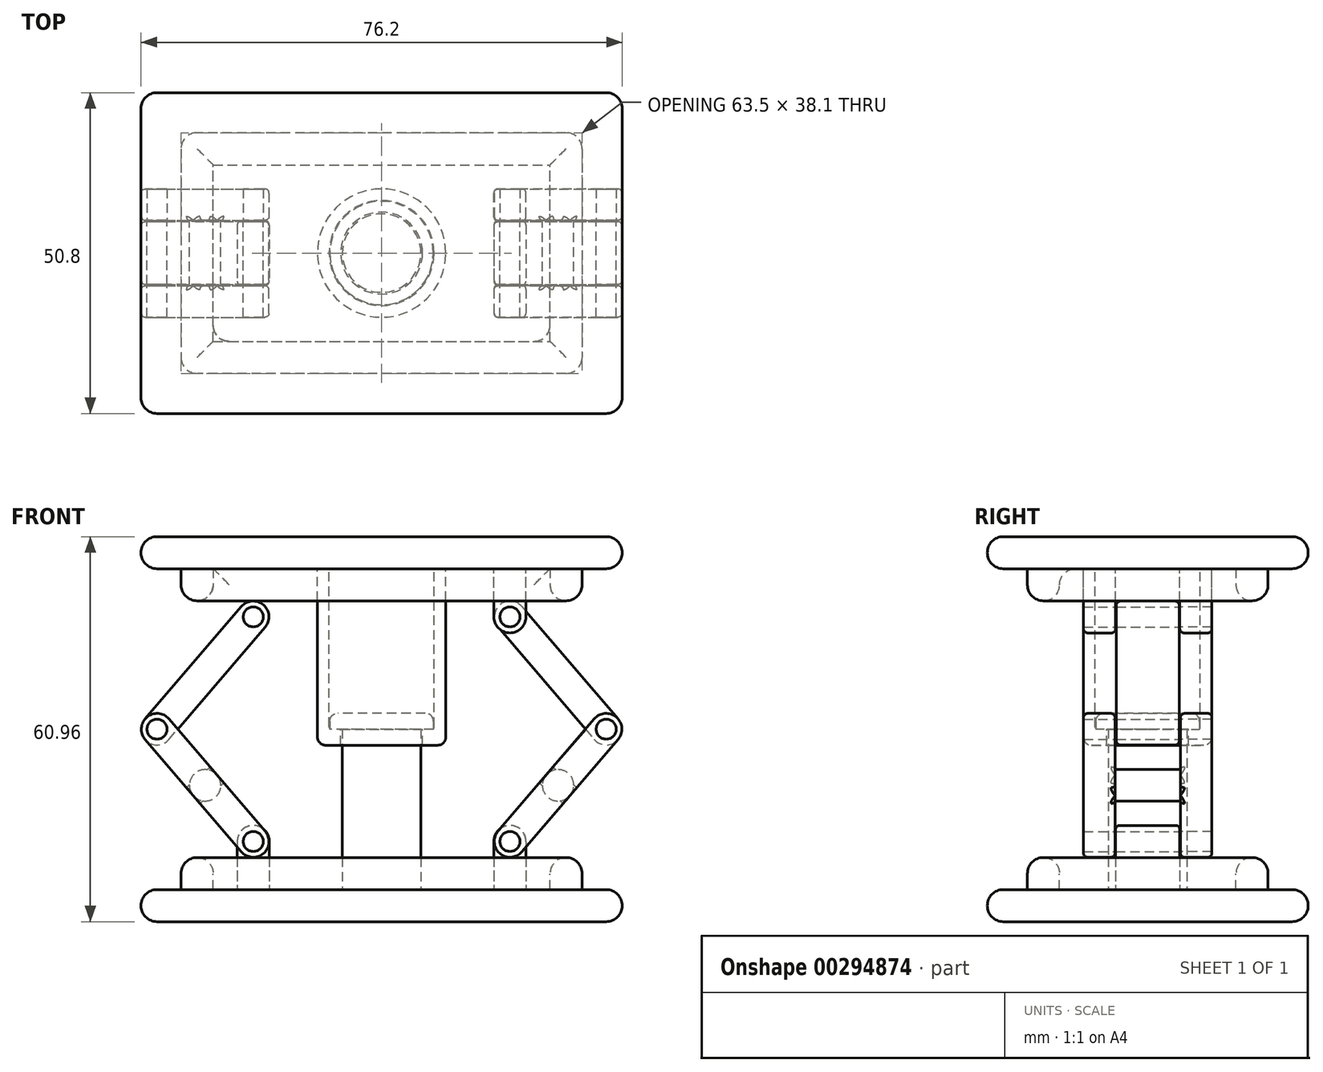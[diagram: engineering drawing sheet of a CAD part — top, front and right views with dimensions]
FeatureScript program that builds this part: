
annotation { "Feature Type Name" : "Feature", "Feature Type Description" : "" }
export const myFeature = defineFeature(function(context is Context, id is Id, definition is map)
    precondition{}
    {
        {
            var Q0;
            Q0=qCreatedBy(makeId("Top.planeOp"),FACE);
            var sketch = newSketch(context, id + "F0", { "sketchPlane" : qUnion([Q0])});
            skLineSegment(sketch, "E0.bottom", {"start": v(-38.1, 25.4) * mm, "end": v(38.1, 25.4) * mm});
            skLineSegment(sketch, "E0.top", {"start": v(-38.1, -25.4) * mm, "end": v(38.1, -25.4) * mm});
            skLineSegment(sketch, "E0.left", {"start": v(-38.1, 25.4) * mm, "end": v(-38.1, -25.4) * mm});
            skLineSegment(sketch, "E0.right", {"start": v(38.1, 25.4) * mm, "end": v(38.1, -25.4) * mm});
            skPoint(sketch, "E0.middle", {"position": v(0, 0) * mm});
            skLineSegment(sketch, "E1.bottom", {"start": v(31.75, 19.05) * mm, "end": v(-31.75, 19.05) * mm});
            skLineSegment(sketch, "E1.top", {"start": v(31.75, -19.05) * mm, "end": v(-31.75, -19.05) * mm});
            skLineSegment(sketch, "E1.left", {"start": v(31.75, 19.05) * mm, "end": v(31.75, -19.05) * mm});
            skLineSegment(sketch, "E1.right", {"start": v(-31.75, 19.05) * mm, "end": v(-31.75, -19.05) * mm});
            skLineSegment(sketch, "E2.bottom", {"start": v(-26.67, -13.97) * mm, "end": v(26.67, -13.97) * mm});
            skLineSegment(sketch, "E2.top", {"start": v(-26.67, 13.97) * mm, "end": v(26.67, 13.97) * mm});
            skLineSegment(sketch, "E2.left", {"start": v(-26.67, -13.97) * mm, "end": v(-26.67, 13.97) * mm});
            skLineSegment(sketch, "E2.right", {"start": v(26.67, -13.97) * mm, "end": v(26.67, 13.97) * mm});
            skSolve(sketch);
        }
        {
            var Q0;
            Q0=makeQuery(id+"F0.imprint","IMPRINT",FACE,{"disambiguationData":[TD([[makeQuery(id+"F0.imprint","IMPRINT",EDGE,{"derivedFrom":sQuery(id+"F0.wireOp",EDGE,"E0.bottom")}),-1.0]])]});
            var Q1;
            Q1=makeQuery(id+"F0.imprint","IMPRINT",FACE,{"disambiguationData":[TD([[makeQuery(id+"F0.imprint","IMPRINT",EDGE,{"derivedFrom":sQuery(id+"F0.wireOp",EDGE,"E2.bottom")}),1.0]])]});
            extrude(context, id + "F1", {"entities" : qUnion([Q0, Q1]), "depth" : 30.48 * mm, "hasSecondDirection" : true, "secondDirectionOppositeDirection" : false, "secondDirectionDepth" : 25.4 * mm});
        }
        {
            var Q0;
            Q0=makeQuery(id+"F0.imprint","IMPRINT",FACE,{"disambiguationData":[TD([[makeQuery(id+"F0.imprint","IMPRINT",EDGE,{"derivedFrom":sQuery(id+"F0.wireOp",EDGE,"E1.bottom")}),1.0]])]});
            extrude(context, id + "F2", {"entities" : qUnion([Q0]), "operationType" : NewBodyOperationType.ADD, "depth" : 30.48 * mm, "hasSecondDirection" : true, "secondDirectionOppositeDirection" : false, "secondDirectionDepth" : 20.32 * mm});
        }
        {
            var Q0;
            Q0=makeQuery(id+"F0.imprint","IMPRINT",FACE,{"disambiguationData":[TD([[makeQuery(id+"F0.imprint","IMPRINT",EDGE,{"derivedFrom":sQuery(id+"F0.wireOp",EDGE,"E0.bottom")}),-1.0]])]});
            var Q1;
            Q1=makeQuery(id+"F0.imprint","IMPRINT",FACE,{"disambiguationData":[TD([[makeQuery(id+"F0.imprint","IMPRINT",EDGE,{"derivedFrom":sQuery(id+"F0.wireOp",EDGE,"E2.bottom")}),1.0]])]});
            extrude(context, id + "F3", {"entities" : qUnion([Q0, Q1]), "oppositeDirection" : true, "depth" : 30.48 * mm, "hasSecondDirection" : true, "secondDirectionOppositeDirection" : true, "secondDirectionDepth" : 25.4 * mm});
        }
        {
            var Q0;
            Q0=makeQuery(id+"F0.imprint","IMPRINT",FACE,{"disambiguationData":[TD([[makeQuery(id+"F0.imprint","IMPRINT",EDGE,{"derivedFrom":sQuery(id+"F0.wireOp",EDGE,"E1.bottom")}),1.0]])]});
            extrude(context, id + "F4", {"entities" : qUnion([Q0]), "operationType" : NewBodyOperationType.ADD, "oppositeDirection" : true, "depth" : 30.48 * mm, "hasSecondDirection" : true, "secondDirectionOppositeDirection" : true, "secondDirectionDepth" : 20.32 * mm});
        }
        {
            var Q0;
            Q0=makeQuery(id+"F1.opExtrude","CAP_FACE",FACE,{"disambiguationData":[OSD([sQuery(id+"F0.wireOp",EDGE,"E2.bottom"),sQuery(id+"F0.wireOp",EDGE,"E2.top"),sQuery(id+"F0.wireOp",EDGE,"E2.left"),sQuery(id+"F0.wireOp",EDGE,"E2.right")])],"isStart":true});
            var sketch = newSketch(context, id + "F5", { "sketchPlane" : qUnion([Q0])});
            skCircle(sketch, "E3", {"center": v(0, 0) * mm, "radius": 10.16 * mm});
            skCircle(sketch, "E4", {"center": v(0, 0) * mm, "radius": 6.48 * mm});
            skCircle(sketch, "E5", {"center": v(0, 0) * mm, "radius": 8.32 * mm});
            skLineSegment(sketch, "E6.bottom", {"start": v(-17.78, 5.08) * mm, "end": v(-22.86, 5.08) * mm});
            skLineSegment(sketch, "E6.top", {"start": v(-17.78, -5.08) * mm, "end": v(-22.86, -5.08) * mm});
            skLineSegment(sketch, "E6.left", {"start": v(-17.78, 5.08) * mm, "end": v(-17.78, -5.08) * mm});
            skLineSegment(sketch, "E6.right", {"start": v(-22.86, 5.08) * mm, "end": v(-22.86, -5.08) * mm});
            skPoint(sketch, "E6.middle", {"position": v(-20.32, 0) * mm});
            skLineSegment(sketch, "E7.bottom", {"start": v(17.78, 5.08) * mm, "end": v(22.86, 5.08) * mm});
            skLineSegment(sketch, "E7.top", {"start": v(17.78, -5.08) * mm, "end": v(22.86, -5.08) * mm});
            skLineSegment(sketch, "E7.left", {"start": v(17.78, 5.08) * mm, "end": v(17.78, -5.08) * mm});
            skLineSegment(sketch, "E7.right", {"start": v(22.86, 5.08) * mm, "end": v(22.86, -5.08) * mm});
            skPoint(sketch, "E7.middle", {"position": v(20.32, 0) * mm});
            skLineSegment(sketch, "E8", {"start": v(-10.16, 0) * mm, "end": v(10.16, 0) * mm});
            skLineSegment(sketch, "E9.bottom", {"start": v(-22.86, 5.08) * mm, "end": v(-17.78, 5.08) * mm});
            skLineSegment(sketch, "E9.top", {"start": v(-22.86, 10.16) * mm, "end": v(-17.78, 10.16) * mm});
            skLineSegment(sketch, "E9.left", {"start": v(-22.86, 5.08) * mm, "end": v(-22.86, 10.16) * mm});
            skLineSegment(sketch, "E9.right", {"start": v(-17.78, 5.08) * mm, "end": v(-17.78, 10.16) * mm});
            skLineSegment(sketch, "E10.bottom", {"start": v(-22.86, -5.08) * mm, "end": v(-17.78, -5.08) * mm});
            skLineSegment(sketch, "E10.top", {"start": v(-22.86, -10.16) * mm, "end": v(-17.78, -10.16) * mm});
            skLineSegment(sketch, "E10.left", {"start": v(-22.86, -5.08) * mm, "end": v(-22.86, -10.16) * mm});
            skLineSegment(sketch, "E10.right", {"start": v(-17.78, -5.08) * mm, "end": v(-17.78, -10.16) * mm});
            skLineSegment(sketch, "E11.top", {"start": v(17.78, -10.16) * mm, "end": v(22.86, -10.16) * mm});
            skLineSegment(sketch, "E11.left", {"start": v(17.78, -5.08) * mm, "end": v(17.78, -10.16) * mm});
            skLineSegment(sketch, "E11.right", {"start": v(22.86, -5.08) * mm, "end": v(22.86, -10.16) * mm});
            skLineSegment(sketch, "E12.top", {"start": v(17.78, 10.16) * mm, "end": v(22.86, 10.16) * mm});
            skLineSegment(sketch, "E12.left", {"start": v(17.78, 5.08) * mm, "end": v(17.78, 10.16) * mm});
            skLineSegment(sketch, "E12.right", {"start": v(22.86, 5.08) * mm, "end": v(22.86, 10.16) * mm});
            skSolve(sketch);
        }
        {
            var Q0;
            Q0=makeQuery(id+"F3.opExtrude","CAP_FACE",FACE,{"disambiguationData":[OSD([sQuery(id+"F0.wireOp",EDGE,"E2.bottom"),sQuery(id+"F0.wireOp",EDGE,"E2.top"),sQuery(id+"F0.wireOp",EDGE,"E2.left"),sQuery(id+"F0.wireOp",EDGE,"E2.right")])],"isStart":true});
            var sketch = newSketch(context, id + "F6", { "sketchPlane" : qUnion([Q0])});
            skCircle(sketch, "E13", {"center": v(0, 0) * mm, "radius": 6.22 * mm});
            skCircle(sketch, "E14", {"center": v(0, 0) * mm, "radius": 8.2 * mm});
            skLineSegment(sketch, "E15.bottom", {"start": v(-22.86, 5.08) * mm, "end": v(-17.78, 5.08) * mm});
            skLineSegment(sketch, "E15.top", {"start": v(-22.86, -5.08) * mm, "end": v(-17.78, -5.08) * mm});
            skLineSegment(sketch, "E15.left", {"start": v(-22.86, 5.08) * mm, "end": v(-22.86, -5.08) * mm});
            skLineSegment(sketch, "E15.right", {"start": v(-17.78, 5.08) * mm, "end": v(-17.78, -5.08) * mm});
            skPoint(sketch, "E15.middle", {"position": v(-20.32, 0) * mm});
            skLineSegment(sketch, "E16.bottom", {"start": v(17.78, 5.08) * mm, "end": v(22.86, 5.08) * mm});
            skLineSegment(sketch, "E16.top", {"start": v(17.78, -5.08) * mm, "end": v(22.86, -5.08) * mm});
            skLineSegment(sketch, "E16.left", {"start": v(17.78, 5.08) * mm, "end": v(17.78, -5.08) * mm});
            skLineSegment(sketch, "E16.right", {"start": v(22.86, 5.08) * mm, "end": v(22.86, -5.08) * mm});
            skPoint(sketch, "E16.middle", {"position": v(20.32, 0) * mm});
            skSolve(sketch);
        }
        {
            var Q0;
            {var subQ0=sQuery(id+"F5.wireOp",EDGE,"E8");var subQ1=sQuery(id+"F5.wireOp",EDGE,"E3");var subQ2=makeQuery(id+"F5.imprint","INTERSECT",VERTEX,{"disambiguationData":[OD(0.0)],"derivedFrom":[subQ1,subQ0]});Q0=makeQuery(id+"F5.imprint","IMPRINT",FACE,{"disambiguationData":[TD([[makeQuery(id+"F5.imprint","IMPRINT",EDGE,{"disambiguationData":[TD([[subQ2,-1.0]])],"derivedFrom":subQ1}),1.0]])]});}
            extrude(context, id + "F7", {"entities" : qUnion([Q0]), "operationType" : NewBodyOperationType.ADD, "depth" : 27.94 * mm});
        }
        {
            var Q0;
            Q0=makeQuery(id+"F6.imprint","IMPRINT",FACE,{"disambiguationData":[TD([[makeQuery(id+"F6.imprint","IMPRINT",EDGE,{"derivedFrom":sQuery(id+"F6.wireOp",EDGE,"E13")}),1.0]])]});
            extrude(context, id + "F8", {"entities" : qUnion([Q0]), "operationType" : NewBodyOperationType.ADD, "depth" : 27.94 * mm});
        }
        {
            var Q0;
            {var subQ0=sQuery(id+"F5.wireOp",EDGE,"E8");var subQ1=sQuery(id+"F5.wireOp",EDGE,"E4");var subQ2=makeQuery(id+"F5.imprint","INTERSECT",VERTEX,{"disambiguationData":[OD(0.0)],"derivedFrom":[subQ1,subQ0]});Q0=makeQuery(id+"F5.imprint","IMPRINT",FACE,{"disambiguationData":[TD([[makeQuery(id+"F5.imprint","IMPRINT",EDGE,{"disambiguationData":[TD([[subQ2,-1.0]])],"derivedFrom":subQ1}),-1.0]])]});}
            extrude(context, id + "F9", {"entities" : qUnion([Q0]), "operationType" : NewBodyOperationType.ADD, "depth" : 27.94 * mm, "hasSecondDirection" : true, "secondDirectionOppositeDirection" : false, "secondDirectionDepth" : 25.4 * mm});
        }
        {
            var Q0;
            Q0=makeQuery(id+"F6.imprint","IMPRINT",FACE,{"disambiguationData":[TD([[makeQuery(id+"F6.imprint","IMPRINT",EDGE,{"derivedFrom":sQuery(id+"F6.wireOp",EDGE,"E13")}),-1.0]])]});
            extrude(context, id + "F10", {"entities" : qUnion([Q0]), "operationType" : NewBodyOperationType.ADD, "depth" : 27.94 * mm, "hasSecondDirection" : true, "secondDirectionOppositeDirection" : false, "secondDirectionDepth" : 25.4 * mm});
        }
        {
            var Q0;
            Q0=makeQuery(id+"F6.imprint","IMPRINT",FACE,{"disambiguationData":[TD([[makeQuery(id+"F6.imprint","IMPRINT",EDGE,{"derivedFrom":sQuery(id+"F6.wireOp",EDGE,"E15.bottom")}),-1.0]])]});
            var Q1;
            Q1=makeQuery(id+"F6.imprint","IMPRINT",FACE,{"disambiguationData":[TD([[makeQuery(id+"F6.imprint","IMPRINT",EDGE,{"derivedFrom":sQuery(id+"F6.wireOp",EDGE,"E16.bottom")}),-1.0]])]});
            extrude(context, id + "F11", {"entities" : qUnion([Q0, Q1]), "operationType" : NewBodyOperationType.ADD, "depth" : 10.16 * mm});
        }
        {
            var Q0;
            Q0=makeQuery(id+"F5.imprint","IMPRINT",FACE,{"disambiguationData":[TD([[makeQuery(id+"F5.imprint","IMPRINT",EDGE,{"derivedFrom":sQuery(id+"F5.wireOp",EDGE,"E9.bottom")}),1.0]])]});
            var Q1;
            Q1=makeQuery(id+"F5.imprint","IMPRINT",FACE,{"disambiguationData":[TD([[makeQuery(id+"F5.imprint","IMPRINT",EDGE,{"derivedFrom":sQuery(id+"F5.wireOp",EDGE,"E10.bottom")}),-1.0]])]});
            var Q2;
            Q2=makeQuery(id+"F5.imprint","IMPRINT",FACE,{"disambiguationData":[TD([[makeQuery(id+"F5.imprint","IMPRINT",EDGE,{"derivedFrom":sQuery(id+"F5.wireOp",EDGE,"E7.top")}),-1.0]])]});
            var Q3;
            Q3=makeQuery(id+"F5.imprint","IMPRINT",FACE,{"disambiguationData":[TD([[makeQuery(id+"F5.imprint","IMPRINT",EDGE,{"derivedFrom":sQuery(id+"F5.wireOp",EDGE,"E7.bottom")}),1.0]])]});
            extrude(context, id + "F12", {"entities" : qUnion([Q0, Q1, Q2, Q3]), "operationType" : NewBodyOperationType.ADD, "depth" : 10.16 * mm});
        }
        {
            var Q0;
            Q0=makeQuery(id+"F11.opExtrude","CAP_EDGE",EDGE,{"disambiguationData":[OSD([sQuery(id+"F6.wireOp",EDGE,"E15.left")])],"isStart":false});
            var Q1;
            Q1=makeQuery(id+"F11.opExtrude","CAP_EDGE",EDGE,{"disambiguationData":[OSD([sQuery(id+"F6.wireOp",EDGE,"E15.right")])],"isStart":false});
            var Q2;
            Q2=makeQuery(id+"F11.opExtrude","CAP_EDGE",EDGE,{"disambiguationData":[OSD([sQuery(id+"F6.wireOp",EDGE,"E16.left")])],"isStart":false});
            var Q3;
            Q3=makeQuery(id+"F11.opExtrude","CAP_EDGE",EDGE,{"disambiguationData":[OSD([sQuery(id+"F6.wireOp",EDGE,"E16.right")])],"isStart":false});
            var Q4;
            Q4=makeQuery(id+"F12.opExtrude","CAP_EDGE",EDGE,{"disambiguationData":[OSD([sQuery(id+"F5.wireOp",EDGE,"E11.left")])],"isStart":false});
            var Q5;
            Q5=makeQuery(id+"F12.opExtrude","CAP_EDGE",EDGE,{"disambiguationData":[OSD([sQuery(id+"F5.wireOp",EDGE,"E12.left")])],"isStart":false});
            var Q6;
            Q6=makeQuery(id+"F12.opExtrude","CAP_EDGE",EDGE,{"disambiguationData":[OSD([sQuery(id+"F5.wireOp",EDGE,"E10.left")])],"isStart":false});
            var Q7;
            Q7=makeQuery(id+"F12.opExtrude","CAP_EDGE",EDGE,{"disambiguationData":[OSD([sQuery(id+"F5.wireOp",EDGE,"E9.left")])],"isStart":false});
            var Q8;
            Q8=makeQuery(id+"F12.opExtrude","CAP_EDGE",EDGE,{"disambiguationData":[OSD([sQuery(id+"F5.wireOp",EDGE,"E10.right")])],"isStart":false});
            var Q9;
            Q9=makeQuery(id+"F12.opExtrude","CAP_EDGE",EDGE,{"disambiguationData":[OSD([sQuery(id+"F5.wireOp",EDGE,"E9.right")])],"isStart":false});
            var Q10;
            Q10=makeQuery(id+"F12.opExtrude","CAP_EDGE",EDGE,{"disambiguationData":[OSD([sQuery(id+"F5.wireOp",EDGE,"E12.right")])],"isStart":false});
            var Q11;
            Q11=makeQuery(id+"F12.opExtrude","CAP_EDGE",EDGE,{"disambiguationData":[OSD([sQuery(id+"F5.wireOp",EDGE,"E11.right")])],"isStart":false});
            fillet(context, id + "F13", {"entities" : qUnion([Q0, Q1, Q2, Q3, Q4, Q5, Q6, Q7, Q8, Q9, Q10, Q11]), "radius" : 2.54 * mm, "tangentPropagation" : true, "allowEdgeOverflow" : false});
        }
        {
            var Q0;
            Q0=qCreatedBy(makeId("Front.planeOp"),FACE);
            var sketch = newSketch(context, id + "F14", { "sketchPlane" : qUnion([Q0])});
            skLineSegment(sketch, "E17.bottom", {"start": v(-20.32, 17.78) * mm, "end": v(20.32, 17.78) * mm});
            skLineSegment(sketch, "E17.top", {"start": v(-20.32, -17.78) * mm, "end": v(20.32, -17.78) * mm});
            skLineSegment(sketch, "E17.left", {"start": v(-20.32, 17.78) * mm, "end": v(-20.32, -17.78) * mm});
            skLineSegment(sketch, "E17.right", {"start": v(20.32, 17.78) * mm, "end": v(20.32, -17.78) * mm});
            skPoint(sketch, "E17.middle", {"position": v(0, 0) * mm});
            skPoint(sketch, "E18", {"position": v(-20.32, 17.78) * mm});
            skPoint(sketch, "E19", {"position": v(20.32, 17.78) * mm});
            skPoint(sketch, "E20", {"position": v(20.32, -17.78) * mm});
            skPoint(sketch, "E21", {"position": v(-20.32, -17.78) * mm});
            skCircle(sketch, "E22", {"center": v(-20.32, 17.78) * mm, "radius": 2.49 * mm});
            skCircle(sketch, "E23", {"center": v(20.32, 17.78) * mm, "radius": 2.49 * mm});
            skCircle(sketch, "E24", {"center": v(20.32, -17.78) * mm, "radius": 2.49 * mm});
            skCircle(sketch, "E25", {"center": v(-20.32, -17.78) * mm, "radius": 2.49 * mm});
            skCircle(sketch, "E26", {"center": v(-35.56, 0) * mm, "radius": 2.49 * mm});
            skCircle(sketch, "E27", {"center": v(35.56, 0) * mm, "radius": 2.49 * mm});
            skLineSegment(sketch, "E28", {"start": v(-22.2, 19.4) * mm, "end": v(-37.45, 1.62) * mm});
            skLineSegment(sketch, "E29", {"start": v(-37.45, -1.62) * mm, "end": v(-22.2, -19.4) * mm});
            skLineSegment(sketch, "E30", {"start": v(-33.67, -1.62) * mm, "end": v(-18.43, 16.16) * mm});
            skLineSegment(sketch, "E31", {"start": v(-33.67, 1.62) * mm, "end": v(-18.43, -16.16) * mm});
            skLineSegment(sketch, "E32", {"start": v(18.43, 16.16) * mm, "end": v(33.67, -1.62) * mm});
            skLineSegment(sketch, "E33", {"start": v(22.2, 19.4) * mm, "end": v(37.45, 1.62) * mm});
            skLineSegment(sketch, "E34", {"start": v(37.45, -1.62) * mm, "end": v(22.2, -19.4) * mm});
            skLineSegment(sketch, "E35", {"start": v(18.43, -16.16) * mm, "end": v(33.67, 1.62) * mm});
            skCircle(sketch, "E36", {"center": v(-27.94, -8.9) * mm, "radius": 2.49 * mm});
            skPoint(sketch, "E36.first.point", {"position": v(-26.05, -7.27) * mm});
            skPoint(sketch, "E36.second.point", {"position": v(-29.83, -10.5) * mm});
            skPoint(sketch, "E36.third.point", {"position": v(-26.05, -10.5) * mm});
            skPoint(sketch, "E36.third.point.positionSnap0", {"position": v(-29.83, -10.5) * mm});
            skPoint(sketch, "E36.third.point.positionSnap1", {"position": v(-26.05, -7.27) * mm});
            skCircle(sketch, "E37", {"center": v(27.94, -8.9) * mm, "radius": 2.49 * mm});
            skPoint(sketch, "E37.first.point", {"position": v(26.05, -7.27) * mm});
            skPoint(sketch, "E37.second.point", {"position": v(29.83, -10.5) * mm});
            skPoint(sketch, "E37.third.point", {"position": v(26.05, -10.5) * mm});
            skPoint(sketch, "E37.third.point.positionSnap0", {"position": v(29.83, -10.5) * mm});
            skPoint(sketch, "E37.third.point.positionSnap1", {"position": v(26.05, -7.27) * mm});
            skSolve(sketch);
        }
        {
            var Q0;
            {var subQ0=sQuery(id+"F5.wireOp",EDGE,"E8");var subQ1=sQuery(id+"F5.wireOp",EDGE,"E3");var subQ2=makeQuery(id+"F5.imprint","INTERSECT",VERTEX,{"disambiguationData":[OD(0.0)],"derivedFrom":[subQ1,subQ0]});Q0=makeQuery(id+"F5.imprint","IMPRINT",FACE,{"disambiguationData":[TD([[makeQuery(id+"F5.imprint","IMPRINT",EDGE,{"disambiguationData":[TD([[subQ2,1.0]])],"derivedFrom":subQ1}),1.0]])]});}
            extrude(context, id + "F15", {"entities" : qUnion([Q0]), "depth" : 27.94 * mm});
        }
        {
            var Q0;
            {var subQ0=sQuery(id+"F5.wireOp",EDGE,"E8");var subQ1=sQuery(id+"F5.wireOp",EDGE,"E4");var subQ2=makeQuery(id+"F5.imprint","INTERSECT",VERTEX,{"disambiguationData":[OD(0.0)],"derivedFrom":[subQ1,subQ0]});Q0=makeQuery(id+"F5.imprint","IMPRINT",FACE,{"disambiguationData":[TD([[makeQuery(id+"F5.imprint","IMPRINT",EDGE,{"disambiguationData":[TD([[subQ2,1.0]])],"derivedFrom":subQ1}),-1.0]])]});}
            extrude(context, id + "F16", {"entities" : qUnion([Q0]), "operationType" : NewBodyOperationType.ADD, "depth" : 27.94 * mm, "hasSecondDirection" : true, "secondDirectionOppositeDirection" : false, "secondDirectionDepth" : 25.4 * mm});
        }
        {
            var Q0;
            {var subQ0=sQuery(id+"F14.wireOp",EDGE,"E28");Q0=makeQuery(id+"F14.imprint","IMPRINT",FACE,{"disambiguationData":[TD([[makeQuery(id+"F14.imprint","IMPRINT",EDGE,{"derivedFrom":subQ0}),1.0]])]});}
            var Q1;
            {var subQ0=sQuery(id+"F14.wireOp",EDGE,"E22");var subQ1=sQuery(id+"F14.wireOp",EDGE,"E17.left");var subQ2=makeQuery(id+"F14.imprint","INTERSECT",VERTEX,{"derivedFrom":[subQ1,subQ0]});Q1=makeQuery(id+"F14.imprint","IMPRINT",FACE,{"disambiguationData":[TD([[makeQuery(id+"F14.imprint","IMPRINT",EDGE,{"disambiguationData":[TD([[subQ2,-1.0]])],"derivedFrom":subQ1}),1.0]])]});}
            var Q2;
            {var subQ0=sQuery(id+"F14.wireOp",EDGE,"E17.left");var subQ1=sQuery(id+"F14.wireOp",EDGE,"E17.bottom");var subQ2=makeQuery(id+"F14.imprint","INTERSECT",VERTEX,{"derivedFrom":[subQ1,subQ0]});Q2=makeQuery(id+"F14.imprint","IMPRINT",FACE,{"disambiguationData":[TD([[makeQuery(id+"F14.imprint","IMPRINT",EDGE,{"disambiguationData":[TD([[subQ2,-1.0]])],"derivedFrom":subQ1}),-1.0]])]});}
            var Q3;
            {var subQ0=sQuery(id+"F14.wireOp",EDGE,"E17.left");var subQ1=sQuery(id+"F14.wireOp",EDGE,"E17.bottom");var subQ2=makeQuery(id+"F14.imprint","INTERSECT",VERTEX,{"derivedFrom":[subQ1,subQ0]});Q3=makeQuery(id+"F14.imprint","IMPRINT",FACE,{"disambiguationData":[TD([[makeQuery(id+"F14.imprint","IMPRINT",EDGE,{"disambiguationData":[TD([[subQ2,-1.0]])],"derivedFrom":subQ1}),1.0]])]});}
            var Q4;
            {var subQ0=sQuery(id+"F14.wireOp",EDGE,"E26");var subQ1=makeQuery(id+"F14.imprint","INTERSECT",VERTEX,{"derivedFrom":[subQ0,sQuery(id+"F14.wireOp",EDGE,"E28")]});Q4=makeQuery(id+"F14.imprint","IMPRINT",FACE,{"disambiguationData":[TD([[makeQuery(id+"F14.imprint","IMPRINT",EDGE,{"disambiguationData":[TD([[subQ1,1.0]])],"derivedFrom":subQ0}),1.0]])]});}
            var Q5;
            {var subQ0=sQuery(id+"F14.wireOp",EDGE,"E30");var subQ1=sQuery(id+"F14.wireOp",EDGE,"E26");var subQ2=makeQuery(id+"F14.imprint","INTERSECT",VERTEX,{"derivedFrom":[subQ1,subQ0]});Q5=makeQuery(id+"F14.imprint","IMPRINT",FACE,{"disambiguationData":[TD([[makeQuery(id+"F14.imprint","IMPRINT",EDGE,{"disambiguationData":[TD([[subQ2,-1.0]])],"derivedFrom":subQ1}),-1.0]])]});}
            var Q6;
            {var subQ0=sQuery(id+"F14.wireOp",EDGE,"E23");var subQ1=sQuery(id+"F14.wireOp",EDGE,"E17.right");var subQ2=makeQuery(id+"F14.imprint","INTERSECT",VERTEX,{"derivedFrom":[subQ1,subQ0]});Q6=makeQuery(id+"F14.imprint","IMPRINT",FACE,{"disambiguationData":[TD([[makeQuery(id+"F14.imprint","IMPRINT",EDGE,{"disambiguationData":[TD([[subQ2,-1.0]])],"derivedFrom":subQ1}),-1.0]])]});}
            var Q7;
            {var subQ5=sQuery(id+"F14.wireOp",EDGE,"E33");Q7=makeQuery(id+"F14.imprint","IMPRINT",FACE,{"disambiguationData":[TD([[makeQuery(id+"F14.imprint","IMPRINT",EDGE,{"derivedFrom":subQ5}),-1.0]])]});}
            var Q8;
            {var subQ0=sQuery(id+"F14.wireOp",EDGE,"E32");var subQ1=sQuery(id+"F14.wireOp",EDGE,"E27");var subQ2=makeQuery(id+"F14.imprint","INTERSECT",VERTEX,{"derivedFrom":[subQ1,subQ0]});Q8=makeQuery(id+"F14.imprint","IMPRINT",FACE,{"disambiguationData":[TD([[makeQuery(id+"F14.imprint","IMPRINT",EDGE,{"disambiguationData":[TD([[subQ2,1.0]])],"derivedFrom":subQ1}),-1.0]])]});}
            var Q9;
            {var subQ0=sQuery(id+"F14.wireOp",EDGE,"E27");var subQ1=makeQuery(id+"F14.imprint","INTERSECT",VERTEX,{"derivedFrom":[subQ0,sQuery(id+"F14.wireOp",EDGE,"E33")]});Q9=makeQuery(id+"F14.imprint","IMPRINT",FACE,{"disambiguationData":[TD([[makeQuery(id+"F14.imprint","IMPRINT",EDGE,{"disambiguationData":[TD([[subQ1,-1.0]])],"derivedFrom":subQ0}),1.0]])]});}
            var Q10;
            {var subQ0=sQuery(id+"F14.wireOp",EDGE,"E17.right");var subQ1=sQuery(id+"F14.wireOp",EDGE,"E17.bottom");var subQ2=makeQuery(id+"F14.imprint","INTERSECT",VERTEX,{"derivedFrom":[subQ1,subQ0]});Q10=makeQuery(id+"F14.imprint","IMPRINT",FACE,{"disambiguationData":[TD([[makeQuery(id+"F14.imprint","IMPRINT",EDGE,{"disambiguationData":[TD([[subQ2,1.0]])],"derivedFrom":subQ1}),1.0]])]});}
            var Q11;
            {var subQ0=sQuery(id+"F14.wireOp",EDGE,"E17.right");var subQ1=sQuery(id+"F14.wireOp",EDGE,"E17.bottom");var subQ2=makeQuery(id+"F14.imprint","INTERSECT",VERTEX,{"derivedFrom":[subQ1,subQ0]});Q11=makeQuery(id+"F14.imprint","IMPRINT",FACE,{"disambiguationData":[TD([[makeQuery(id+"F14.imprint","IMPRINT",EDGE,{"disambiguationData":[TD([[subQ2,1.0]])],"derivedFrom":subQ1}),-1.0]])]});}
            extrude(context, id + "F17", {"entities" : qUnion([Q0, Q1, Q2, Q3, Q4, Q5, Q6, Q7, Q8, Q9, Q10, Q11]), "depth" : 9.96 * mm, "symmetric" : true});
        }
        {
            var Q0;
            {var subQ0=sQuery(id+"F14.wireOp",EDGE,"E36");var subQ1=makeQuery(id+"F14.imprint","INTERSECT",VERTEX,{"derivedFrom":[sQuery(id+"F14.wireOp",EDGE,"E29"),subQ0]});Q0=makeQuery(id+"F14.imprint","IMPRINT",FACE,{"disambiguationData":[TD([[makeQuery(id+"F14.imprint","IMPRINT",EDGE,{"disambiguationData":[TD([[subQ1,1.0]])],"derivedFrom":subQ0}),1.0]])]});}
            var Q1;
            {var subQ0=sQuery(id+"F14.wireOp",EDGE,"E31");var subQ1=sQuery(id+"F14.wireOp",EDGE,"E17.left");var subQ2=makeQuery(id+"F14.imprint","INTERSECT",VERTEX,{"derivedFrom":[subQ1,subQ0]});Q1=makeQuery(id+"F14.imprint","IMPRINT",FACE,{"disambiguationData":[TD([[makeQuery(id+"F14.imprint","IMPRINT",EDGE,{"disambiguationData":[TD([[subQ2,-1.0]])],"derivedFrom":subQ1}),-1.0]])]});}
            var Q2;
            {var subQ0=sQuery(id+"F14.wireOp",EDGE,"E26");var subQ1=makeQuery(id+"F14.imprint","INTERSECT",VERTEX,{"derivedFrom":[subQ0,sQuery(id+"F14.wireOp",EDGE,"E28")]});Q2=makeQuery(id+"F14.imprint","IMPRINT",FACE,{"disambiguationData":[TD([[makeQuery(id+"F14.imprint","IMPRINT",EDGE,{"disambiguationData":[TD([[subQ1,1.0]])],"derivedFrom":subQ0}),1.0]])]});}
            var Q3;
            {var subQ5=sQuery(id+"F14.wireOp",EDGE,"E26");var subQ7=sQuery(id+"F14.wireOp",EDGE,"E29");var subQ8=makeQuery(id+"F14.imprint","INTERSECT",VERTEX,{"derivedFrom":[subQ5,subQ7]});Q3=makeQuery(id+"F14.imprint","IMPRINT",FACE,{"disambiguationData":[TD([[makeQuery(id+"F14.imprint","IMPRINT",EDGE,{"disambiguationData":[TD([[subQ8,-1.0]])],"derivedFrom":subQ5}),-1.0]])]});}
            var Q4;
            {var subQ0=sQuery(id+"F14.wireOp",EDGE,"E30");var subQ1=sQuery(id+"F14.wireOp",EDGE,"E26");var subQ2=makeQuery(id+"F14.imprint","INTERSECT",VERTEX,{"derivedFrom":[subQ1,subQ0]});Q4=makeQuery(id+"F14.imprint","IMPRINT",FACE,{"disambiguationData":[TD([[makeQuery(id+"F14.imprint","IMPRINT",EDGE,{"disambiguationData":[TD([[subQ2,-1.0]])],"derivedFrom":subQ1}),-1.0]])]});}
            var Q5;
            {var subQ0=sQuery(id+"F14.wireOp",EDGE,"E17.right");var subQ1=sQuery(id+"F14.wireOp",EDGE,"E17.top");var subQ2=makeQuery(id+"F14.imprint","INTERSECT",VERTEX,{"derivedFrom":[subQ1,subQ0]});Q5=makeQuery(id+"F14.imprint","IMPRINT",FACE,{"disambiguationData":[TD([[makeQuery(id+"F14.imprint","IMPRINT",EDGE,{"disambiguationData":[TD([[subQ2,1.0]])],"derivedFrom":subQ1}),-1.0]])]});}
            var Q6;
            {var subQ0=sQuery(id+"F14.wireOp",EDGE,"E17.right");var subQ1=sQuery(id+"F14.wireOp",EDGE,"E17.top");var subQ2=makeQuery(id+"F14.imprint","INTERSECT",VERTEX,{"derivedFrom":[subQ1,subQ0]});Q6=makeQuery(id+"F14.imprint","IMPRINT",FACE,{"disambiguationData":[TD([[makeQuery(id+"F14.imprint","IMPRINT",EDGE,{"disambiguationData":[TD([[subQ2,1.0]])],"derivedFrom":subQ1}),1.0]])]});}
            var Q7;
            {var subQ0=sQuery(id+"F14.wireOp",EDGE,"E35");var subQ1=sQuery(id+"F14.wireOp",EDGE,"E17.right");var subQ2=makeQuery(id+"F14.imprint","INTERSECT",VERTEX,{"derivedFrom":[subQ1,subQ0]});Q7=makeQuery(id+"F14.imprint","IMPRINT",FACE,{"disambiguationData":[TD([[makeQuery(id+"F14.imprint","IMPRINT",EDGE,{"disambiguationData":[TD([[subQ2,-1.0]])],"derivedFrom":subQ1}),-1.0]])]});}
            var Q8;
            {var subQ5=sQuery(id+"F14.wireOp",EDGE,"E35");var subQ6=sQuery(id+"F14.wireOp",EDGE,"E17.right");var subQ7=makeQuery(id+"F14.imprint","INTERSECT",VERTEX,{"derivedFrom":[subQ6,subQ5]});Q8=makeQuery(id+"F14.imprint","IMPRINT",FACE,{"disambiguationData":[TD([[makeQuery(id+"F14.imprint","IMPRINT",EDGE,{"disambiguationData":[TD([[subQ7,-1.0]])],"derivedFrom":subQ6}),1.0]])]});}
            var Q9;
            {var subQ0=sQuery(id+"F14.wireOp",EDGE,"E37");var subQ1=makeQuery(id+"F14.imprint","INTERSECT",VERTEX,{"derivedFrom":[sQuery(id+"F14.wireOp",EDGE,"E34"),subQ0]});Q9=makeQuery(id+"F14.imprint","IMPRINT",FACE,{"disambiguationData":[TD([[makeQuery(id+"F14.imprint","IMPRINT",EDGE,{"disambiguationData":[TD([[subQ1,1.0]])],"derivedFrom":subQ0}),1.0]])]});}
            var Q10;
            {var subQ1=sQuery(id+"F14.wireOp",EDGE,"E27");var subQ5=sQuery(id+"F14.wireOp",EDGE,"E32");var subQ6=makeQuery(id+"F14.imprint","INTERSECT",VERTEX,{"derivedFrom":[subQ1,subQ5]});Q10=makeQuery(id+"F14.imprint","IMPRINT",FACE,{"disambiguationData":[TD([[makeQuery(id+"F14.imprint","IMPRINT",EDGE,{"disambiguationData":[TD([[subQ6,-1.0]])],"derivedFrom":subQ1}),-1.0]])]});}
            var Q11;
            {var subQ0=sQuery(id+"F14.wireOp",EDGE,"E32");var subQ1=sQuery(id+"F14.wireOp",EDGE,"E27");var subQ2=makeQuery(id+"F14.imprint","INTERSECT",VERTEX,{"derivedFrom":[subQ1,subQ0]});Q11=makeQuery(id+"F14.imprint","IMPRINT",FACE,{"disambiguationData":[TD([[makeQuery(id+"F14.imprint","IMPRINT",EDGE,{"disambiguationData":[TD([[subQ2,1.0]])],"derivedFrom":subQ1}),-1.0]])]});}
            var Q12;
            {var subQ0=sQuery(id+"F14.wireOp",EDGE,"E27");var subQ1=makeQuery(id+"F14.imprint","INTERSECT",VERTEX,{"derivedFrom":[subQ0,sQuery(id+"F14.wireOp",EDGE,"E33")]});Q12=makeQuery(id+"F14.imprint","IMPRINT",FACE,{"disambiguationData":[TD([[makeQuery(id+"F14.imprint","IMPRINT",EDGE,{"disambiguationData":[TD([[subQ1,-1.0]])],"derivedFrom":subQ0}),1.0]])]});}
            var Q13;
            {var subQ0=sQuery(id+"F14.wireOp",EDGE,"E17.left");var subQ1=sQuery(id+"F14.wireOp",EDGE,"E17.top");var subQ2=makeQuery(id+"F14.imprint","INTERSECT",VERTEX,{"derivedFrom":[subQ1,subQ0]});Q13=makeQuery(id+"F14.imprint","IMPRINT",FACE,{"disambiguationData":[TD([[makeQuery(id+"F14.imprint","IMPRINT",EDGE,{"disambiguationData":[TD([[subQ2,-1.0]])],"derivedFrom":subQ1}),-1.0]])]});}
            var Q14;
            {var subQ0=sQuery(id+"F14.wireOp",EDGE,"E17.left");var subQ1=sQuery(id+"F14.wireOp",EDGE,"E17.top");var subQ2=makeQuery(id+"F14.imprint","INTERSECT",VERTEX,{"derivedFrom":[subQ1,subQ0]});Q14=makeQuery(id+"F14.imprint","IMPRINT",FACE,{"disambiguationData":[TD([[makeQuery(id+"F14.imprint","IMPRINT",EDGE,{"disambiguationData":[TD([[subQ2,-1.0]])],"derivedFrom":subQ1}),1.0]])]});}
            var Q15;
            {var subQ0=sQuery(id+"F14.wireOp",EDGE,"E31");var subQ1=sQuery(id+"F14.wireOp",EDGE,"E17.left");var subQ2=makeQuery(id+"F14.imprint","INTERSECT",VERTEX,{"derivedFrom":[subQ1,subQ0]});Q15=makeQuery(id+"F14.imprint","IMPRINT",FACE,{"disambiguationData":[TD([[makeQuery(id+"F14.imprint","IMPRINT",EDGE,{"disambiguationData":[TD([[subQ2,-1.0]])],"derivedFrom":subQ1}),1.0]])]});}
            extrude(context, id + "F18", {"entities" : qUnion([Q0, Q1, Q2, Q3, Q4, Q5, Q6, Q7, Q8, Q9, Q10, Q11, Q12, Q13, Q14, Q15]), "depth" : 10.16 * mm, "hasSecondDirection" : true, "secondDirectionOppositeDirection" : false, "secondDirectionDepth" : 5.18 * mm});
        }
        {
            var Q0;
            {var subQ5=sQuery(id+"F14.wireOp",EDGE,"E26");var subQ7=sQuery(id+"F14.wireOp",EDGE,"E29");var subQ8=makeQuery(id+"F14.imprint","INTERSECT",VERTEX,{"derivedFrom":[subQ5,subQ7]});Q0=makeQuery(id+"F14.imprint","IMPRINT",FACE,{"disambiguationData":[TD([[makeQuery(id+"F14.imprint","IMPRINT",EDGE,{"disambiguationData":[TD([[subQ8,-1.0]])],"derivedFrom":subQ5}),-1.0]])]});}
            var Q1;
            {var subQ0=sQuery(id+"F14.wireOp",EDGE,"E26");var subQ1=makeQuery(id+"F14.imprint","INTERSECT",VERTEX,{"derivedFrom":[subQ0,sQuery(id+"F14.wireOp",EDGE,"E28")]});Q1=makeQuery(id+"F14.imprint","IMPRINT",FACE,{"disambiguationData":[TD([[makeQuery(id+"F14.imprint","IMPRINT",EDGE,{"disambiguationData":[TD([[subQ1,1.0]])],"derivedFrom":subQ0}),1.0]])]});}
            var Q2;
            {var subQ0=sQuery(id+"F14.wireOp",EDGE,"E30");var subQ1=sQuery(id+"F14.wireOp",EDGE,"E26");var subQ2=makeQuery(id+"F14.imprint","INTERSECT",VERTEX,{"derivedFrom":[subQ1,subQ0]});Q2=makeQuery(id+"F14.imprint","IMPRINT",FACE,{"disambiguationData":[TD([[makeQuery(id+"F14.imprint","IMPRINT",EDGE,{"disambiguationData":[TD([[subQ2,-1.0]])],"derivedFrom":subQ1}),-1.0]])]});}
            var Q3;
            {var subQ0=sQuery(id+"F14.wireOp",EDGE,"E36");var subQ1=makeQuery(id+"F14.imprint","INTERSECT",VERTEX,{"derivedFrom":[sQuery(id+"F14.wireOp",EDGE,"E29"),subQ0]});Q3=makeQuery(id+"F14.imprint","IMPRINT",FACE,{"disambiguationData":[TD([[makeQuery(id+"F14.imprint","IMPRINT",EDGE,{"disambiguationData":[TD([[subQ1,1.0]])],"derivedFrom":subQ0}),1.0]])]});}
            var Q4;
            {var subQ0=sQuery(id+"F14.wireOp",EDGE,"E31");var subQ1=sQuery(id+"F14.wireOp",EDGE,"E17.left");var subQ2=makeQuery(id+"F14.imprint","INTERSECT",VERTEX,{"derivedFrom":[subQ1,subQ0]});Q4=makeQuery(id+"F14.imprint","IMPRINT",FACE,{"disambiguationData":[TD([[makeQuery(id+"F14.imprint","IMPRINT",EDGE,{"disambiguationData":[TD([[subQ2,-1.0]])],"derivedFrom":subQ1}),-1.0]])]});}
            var Q5;
            {var subQ0=sQuery(id+"F14.wireOp",EDGE,"E17.left");var subQ1=sQuery(id+"F14.wireOp",EDGE,"E17.top");var subQ2=makeQuery(id+"F14.imprint","INTERSECT",VERTEX,{"derivedFrom":[subQ1,subQ0]});Q5=makeQuery(id+"F14.imprint","IMPRINT",FACE,{"disambiguationData":[TD([[makeQuery(id+"F14.imprint","IMPRINT",EDGE,{"disambiguationData":[TD([[subQ2,-1.0]])],"derivedFrom":subQ1}),1.0]])]});}
            var Q6;
            {var subQ0=sQuery(id+"F14.wireOp",EDGE,"E17.left");var subQ1=sQuery(id+"F14.wireOp",EDGE,"E17.top");var subQ2=makeQuery(id+"F14.imprint","INTERSECT",VERTEX,{"derivedFrom":[subQ1,subQ0]});Q6=makeQuery(id+"F14.imprint","IMPRINT",FACE,{"disambiguationData":[TD([[makeQuery(id+"F14.imprint","IMPRINT",EDGE,{"disambiguationData":[TD([[subQ2,-1.0]])],"derivedFrom":subQ1}),-1.0]])]});}
            var Q7;
            {var subQ0=sQuery(id+"F14.wireOp",EDGE,"E31");var subQ1=sQuery(id+"F14.wireOp",EDGE,"E17.left");var subQ2=makeQuery(id+"F14.imprint","INTERSECT",VERTEX,{"derivedFrom":[subQ1,subQ0]});Q7=makeQuery(id+"F14.imprint","IMPRINT",FACE,{"disambiguationData":[TD([[makeQuery(id+"F14.imprint","IMPRINT",EDGE,{"disambiguationData":[TD([[subQ2,-1.0]])],"derivedFrom":subQ1}),1.0]])]});}
            var Q8;
            {var subQ0=sQuery(id+"F14.wireOp",EDGE,"E35");var subQ1=sQuery(id+"F14.wireOp",EDGE,"E17.right");var subQ2=makeQuery(id+"F14.imprint","INTERSECT",VERTEX,{"derivedFrom":[subQ1,subQ0]});Q8=makeQuery(id+"F14.imprint","IMPRINT",FACE,{"disambiguationData":[TD([[makeQuery(id+"F14.imprint","IMPRINT",EDGE,{"disambiguationData":[TD([[subQ2,-1.0]])],"derivedFrom":subQ1}),-1.0]])]});}
            var Q9;
            {var subQ0=sQuery(id+"F14.wireOp",EDGE,"E17.right");var subQ1=sQuery(id+"F14.wireOp",EDGE,"E17.top");var subQ2=makeQuery(id+"F14.imprint","INTERSECT",VERTEX,{"derivedFrom":[subQ1,subQ0]});Q9=makeQuery(id+"F14.imprint","IMPRINT",FACE,{"disambiguationData":[TD([[makeQuery(id+"F14.imprint","IMPRINT",EDGE,{"disambiguationData":[TD([[subQ2,1.0]])],"derivedFrom":subQ1}),1.0]])]});}
            var Q10;
            {var subQ0=sQuery(id+"F14.wireOp",EDGE,"E17.right");var subQ1=sQuery(id+"F14.wireOp",EDGE,"E17.top");var subQ2=makeQuery(id+"F14.imprint","INTERSECT",VERTEX,{"derivedFrom":[subQ1,subQ0]});Q10=makeQuery(id+"F14.imprint","IMPRINT",FACE,{"disambiguationData":[TD([[makeQuery(id+"F14.imprint","IMPRINT",EDGE,{"disambiguationData":[TD([[subQ2,1.0]])],"derivedFrom":subQ1}),-1.0]])]});}
            var Q11;
            {var subQ5=sQuery(id+"F14.wireOp",EDGE,"E35");var subQ6=sQuery(id+"F14.wireOp",EDGE,"E17.right");var subQ7=makeQuery(id+"F14.imprint","INTERSECT",VERTEX,{"derivedFrom":[subQ6,subQ5]});Q11=makeQuery(id+"F14.imprint","IMPRINT",FACE,{"disambiguationData":[TD([[makeQuery(id+"F14.imprint","IMPRINT",EDGE,{"disambiguationData":[TD([[subQ7,-1.0]])],"derivedFrom":subQ6}),1.0]])]});}
            var Q12;
            {var subQ0=sQuery(id+"F14.wireOp",EDGE,"E37");var subQ1=makeQuery(id+"F14.imprint","INTERSECT",VERTEX,{"derivedFrom":[sQuery(id+"F14.wireOp",EDGE,"E34"),subQ0]});Q12=makeQuery(id+"F14.imprint","IMPRINT",FACE,{"disambiguationData":[TD([[makeQuery(id+"F14.imprint","IMPRINT",EDGE,{"disambiguationData":[TD([[subQ1,1.0]])],"derivedFrom":subQ0}),1.0]])]});}
            var Q13;
            {var subQ1=sQuery(id+"F14.wireOp",EDGE,"E27");var subQ5=sQuery(id+"F14.wireOp",EDGE,"E32");var subQ6=makeQuery(id+"F14.imprint","INTERSECT",VERTEX,{"derivedFrom":[subQ1,subQ5]});Q13=makeQuery(id+"F14.imprint","IMPRINT",FACE,{"disambiguationData":[TD([[makeQuery(id+"F14.imprint","IMPRINT",EDGE,{"disambiguationData":[TD([[subQ6,-1.0]])],"derivedFrom":subQ1}),-1.0]])]});}
            var Q14;
            {var subQ0=sQuery(id+"F14.wireOp",EDGE,"E32");var subQ1=sQuery(id+"F14.wireOp",EDGE,"E27");var subQ2=makeQuery(id+"F14.imprint","INTERSECT",VERTEX,{"derivedFrom":[subQ1,subQ0]});Q14=makeQuery(id+"F14.imprint","IMPRINT",FACE,{"disambiguationData":[TD([[makeQuery(id+"F14.imprint","IMPRINT",EDGE,{"disambiguationData":[TD([[subQ2,1.0]])],"derivedFrom":subQ1}),-1.0]])]});}
            var Q15;
            {var subQ0=sQuery(id+"F14.wireOp",EDGE,"E27");var subQ1=makeQuery(id+"F14.imprint","INTERSECT",VERTEX,{"derivedFrom":[subQ0,sQuery(id+"F14.wireOp",EDGE,"E33")]});Q15=makeQuery(id+"F14.imprint","IMPRINT",FACE,{"disambiguationData":[TD([[makeQuery(id+"F14.imprint","IMPRINT",EDGE,{"disambiguationData":[TD([[subQ1,-1.0]])],"derivedFrom":subQ0}),1.0]])]});}
            extrude(context, id + "F19", {"entities" : qUnion([Q0, Q1, Q2, Q3, Q4, Q5, Q6, Q7, Q8, Q9, Q10, Q11, Q12, Q13, Q14, Q15]), "oppositeDirection" : true, "depth" : 10.16 * mm, "hasSecondDirection" : true, "secondDirectionOppositeDirection" : true, "secondDirectionDepth" : 5.18 * mm});
        }
        {
            var Q0;
            Q0=sQuery(id+"F14.wireOp",VERTEX,"E18");
            var Q1;
            Q1=sQuery(id+"F14.wireOp",VERTEX,"E19");
            var Q2;
            Q2=sQuery(id+"F14.wireOp",VERTEX,"E20");
            var Q3;
            Q3=sQuery(id+"F14.wireOp",VERTEX,"E21");
            var Q4;
            Q4=sQuery(id+"F14.wireOp",VERTEX,"E26.center");
            var Q5;
            Q5=sQuery(id+"F14.wireOp",VERTEX,"E27.center");
            var Q6;
            Q6=makeQuery(id+"F1.opExtrude","SWEPT_BODY",BODY,{"disambiguationData":[OSD([sQuery(id+"F0.wireOp",EDGE,"E0.bottom"),sQuery(id+"F0.wireOp",EDGE,"E0.top"),sQuery(id+"F0.wireOp",EDGE,"E0.left"),sQuery(id+"F0.wireOp",EDGE,"E0.right"),sQuery(id+"F0.wireOp",EDGE,"E1.bottom"),sQuery(id+"F0.wireOp",EDGE,"E1.top"),sQuery(id+"F0.wireOp",EDGE,"E1.left"),sQuery(id+"F0.wireOp",EDGE,"E1.right")])]});
            var Q7;
            Q7=makeQuery(id+"F17.opExtrude","SWEPT_BODY",BODY,{"disambiguationData":[OSD([sQuery(id+"F14.wireOp",EDGE,"E23"),sQuery(id+"F14.wireOp",EDGE,"E27"),sQuery(id+"F14.wireOp",EDGE,"E32"),sQuery(id+"F14.wireOp",EDGE,"E33")])]});
            var Q8;
            Q8=makeQuery(id+"F18.opExtrude","SWEPT_BODY",BODY,{"disambiguationData":[OSD([sQuery(id+"F14.wireOp",EDGE,"E24"),sQuery(id+"F14.wireOp",EDGE,"E27"),sQuery(id+"F14.wireOp",EDGE,"E34"),sQuery(id+"F14.wireOp",EDGE,"E35")])]});
            var Q9;
            Q9=makeQuery(id+"F3.opExtrude","SWEPT_BODY",BODY,{"disambiguationData":[OSD([sQuery(id+"F0.wireOp",EDGE,"E0.bottom"),sQuery(id+"F0.wireOp",EDGE,"E0.top"),sQuery(id+"F0.wireOp",EDGE,"E0.left"),sQuery(id+"F0.wireOp",EDGE,"E0.right"),sQuery(id+"F0.wireOp",EDGE,"E1.bottom"),sQuery(id+"F0.wireOp",EDGE,"E1.top"),sQuery(id+"F0.wireOp",EDGE,"E1.left"),sQuery(id+"F0.wireOp",EDGE,"E1.right")])]});
            var Q10;
            Q10=makeQuery(id+"F18.opExtrude","SWEPT_BODY",BODY,{"disambiguationData":[OSD([sQuery(id+"F14.wireOp",EDGE,"E25"),sQuery(id+"F14.wireOp",EDGE,"E26"),sQuery(id+"F14.wireOp",EDGE,"E29"),sQuery(id+"F14.wireOp",EDGE,"E31")])]});
            var Q11;
            Q11=makeQuery(id+"F17.opExtrude","SWEPT_BODY",BODY,{"disambiguationData":[OSD([sQuery(id+"F14.wireOp",EDGE,"E22"),sQuery(id+"F14.wireOp",EDGE,"E26"),sQuery(id+"F14.wireOp",EDGE,"E28"),sQuery(id+"F14.wireOp",EDGE,"E30")])]});
            hole(context, id + "F20", {"style" : HoleStyle.SIMPLE, "endStyle" : HoleEndStyle.THROUGH, "oppositeDirection" : true, "holeDiameter" : 3.17 * mm, "tappedDepth" : 12.7 * mm, "tapClearance" : 3, "locations" : qUnion([Q0, Q1, Q2, Q3, Q4, Q5]), "scope" : qUnion([Q6, Q7, Q8, Q9, Q10, Q11])});
        }
        {
            var Q0;
            Q0=sQuery(id+"F14.wireOp",VERTEX,"E18");
            var Q1;
            Q1=sQuery(id+"F14.wireOp",VERTEX,"E21");
            var Q2;
            Q2=sQuery(id+"F14.wireOp",VERTEX,"E20");
            var Q3;
            Q3=sQuery(id+"F14.wireOp",VERTEX,"E19");
            var Q4;
            Q4=sQuery(id+"F14.wireOp",VERTEX,"E26.center");
            var Q5;
            Q5=sQuery(id+"F14.wireOp",VERTEX,"E27.center");
            var Q6;
            Q6=makeQuery(id+"F1.opExtrude","SWEPT_BODY",BODY,{"disambiguationData":[OSD([sQuery(id+"F0.wireOp",EDGE,"E0.bottom"),sQuery(id+"F0.wireOp",EDGE,"E0.top"),sQuery(id+"F0.wireOp",EDGE,"E0.left"),sQuery(id+"F0.wireOp",EDGE,"E0.right"),sQuery(id+"F0.wireOp",EDGE,"E1.bottom"),sQuery(id+"F0.wireOp",EDGE,"E1.top"),sQuery(id+"F0.wireOp",EDGE,"E1.left"),sQuery(id+"F0.wireOp",EDGE,"E1.right")])]});
            var Q7;
            Q7=makeQuery(id+"F17.opExtrude","SWEPT_BODY",BODY,{"disambiguationData":[OSD([sQuery(id+"F14.wireOp",EDGE,"E23"),sQuery(id+"F14.wireOp",EDGE,"E27"),sQuery(id+"F14.wireOp",EDGE,"E32"),sQuery(id+"F14.wireOp",EDGE,"E33")])]});
            var Q8;
            Q8=makeQuery(id+"F19.opExtrude","SWEPT_BODY",BODY,{"disambiguationData":[OSD([sQuery(id+"F14.wireOp",EDGE,"E24"),sQuery(id+"F14.wireOp",EDGE,"E27"),sQuery(id+"F14.wireOp",EDGE,"E34"),sQuery(id+"F14.wireOp",EDGE,"E35")])]});
            var Q9;
            Q9=makeQuery(id+"F3.opExtrude","SWEPT_BODY",BODY,{"disambiguationData":[OSD([sQuery(id+"F0.wireOp",EDGE,"E0.bottom"),sQuery(id+"F0.wireOp",EDGE,"E0.top"),sQuery(id+"F0.wireOp",EDGE,"E0.left"),sQuery(id+"F0.wireOp",EDGE,"E0.right"),sQuery(id+"F0.wireOp",EDGE,"E1.bottom"),sQuery(id+"F0.wireOp",EDGE,"E1.top"),sQuery(id+"F0.wireOp",EDGE,"E1.left"),sQuery(id+"F0.wireOp",EDGE,"E1.right")])]});
            var Q10;
            Q10=makeQuery(id+"F19.opExtrude","SWEPT_BODY",BODY,{"disambiguationData":[OSD([sQuery(id+"F14.wireOp",EDGE,"E25"),sQuery(id+"F14.wireOp",EDGE,"E26"),sQuery(id+"F14.wireOp",EDGE,"E29"),sQuery(id+"F14.wireOp",EDGE,"E31")])]});
            var Q11;
            Q11=makeQuery(id+"F17.opExtrude","SWEPT_BODY",BODY,{"disambiguationData":[OSD([sQuery(id+"F14.wireOp",EDGE,"E22"),sQuery(id+"F14.wireOp",EDGE,"E26"),sQuery(id+"F14.wireOp",EDGE,"E28"),sQuery(id+"F14.wireOp",EDGE,"E30")])]});
            hole(context, id + "F21", {"style" : HoleStyle.SIMPLE, "endStyle" : HoleEndStyle.THROUGH, "holeDiameter" : 3.17 * mm, "tappedDepth" : 12.7 * mm, "tapClearance" : 3, "locations" : qUnion([Q0, Q1, Q2, Q3, Q4, Q5]), "scope" : qUnion([Q6, Q7, Q8, Q9, Q10, Q11])});
        }
        {
            var Q0;
            {var subQ0=sQuery(id+"F14.wireOp",EDGE,"E36");var subQ1=makeQuery(id+"F14.imprint","INTERSECT",VERTEX,{"derivedFrom":[sQuery(id+"F14.wireOp",EDGE,"E29"),subQ0]});Q0=makeQuery(id+"F14.imprint","IMPRINT",FACE,{"disambiguationData":[TD([[makeQuery(id+"F14.imprint","IMPRINT",EDGE,{"disambiguationData":[TD([[subQ1,1.0]])],"derivedFrom":subQ0}),1.0]])]});}
            var Q1;
            {var subQ0=sQuery(id+"F14.wireOp",EDGE,"E37");var subQ1=makeQuery(id+"F14.imprint","INTERSECT",VERTEX,{"derivedFrom":[sQuery(id+"F14.wireOp",EDGE,"E34"),subQ0]});Q1=makeQuery(id+"F14.imprint","IMPRINT",FACE,{"disambiguationData":[TD([[makeQuery(id+"F14.imprint","IMPRINT",EDGE,{"disambiguationData":[TD([[subQ1,1.0]])],"derivedFrom":subQ0}),1.0]])]});}
            extrude(context, id + "F22", {"entities" : qUnion([Q0, Q1]), "operationType" : NewBodyOperationType.ADD, "depth" : 10.37 * mm, "symmetric" : true});
        }
        {
            var Q0;
            Q0=makeQuery(id+"F10.opExtrude","CAP_EDGE",EDGE,{"disambiguationData":[OSD([sQuery(id+"F6.wireOp",EDGE,"E14")])],"isStart":true});
            var Q1;
            Q1=makeQuery(id+"F16.opExtrude","CAP_EDGE",EDGE,{"disambiguationData":[OSD([sQuery(id+"F5.wireOp",EDGE,"E5")])],"isStart":true});
            var Q2;
            Q2=makeQuery(id+"F9.opExtrude","CAP_EDGE",EDGE,{"disambiguationData":[OSD([sQuery(id+"F5.wireOp",EDGE,"E5")])],"isStart":true});
            fillet(context, id + "F23", {"entities" : qUnion([Q0, Q1, Q2]), "radius" : 0.64 * mm, "tangentPropagation" : true, "allowEdgeOverflow" : false});
        }
        {
            var Q0;
            Q0=makeQuery(id+"F1.opExtrude","SWEPT_FACE",FACE,{"disambiguationData":[OSD([sQuery(id+"F0.wireOp",EDGE,"E0.bottom")])]});
            var Q1;
            Q1=makeQuery(id+"F1.opExtrude","SWEPT_FACE",FACE,{"disambiguationData":[OSD([sQuery(id+"F0.wireOp",EDGE,"E0.right")])]});
            var Q2;
            Q2=makeQuery(id+"F1.opExtrude","SWEPT_FACE",FACE,{"disambiguationData":[OSD([sQuery(id+"F0.wireOp",EDGE,"E0.top")])]});
            var Q3;
            Q3=makeQuery(id+"F1.opExtrude","SWEPT_FACE",FACE,{"disambiguationData":[OSD([sQuery(id+"F0.wireOp",EDGE,"E0.left")])]});
            var Q4;
            Q4=makeQuery(id+"F3.opExtrude","SWEPT_FACE",FACE,{"disambiguationData":[OSD([sQuery(id+"F0.wireOp",EDGE,"E0.left")])]});
            var Q5;
            Q5=makeQuery(id+"F3.opExtrude","SWEPT_FACE",FACE,{"disambiguationData":[OSD([sQuery(id+"F0.wireOp",EDGE,"E0.bottom")])]});
            var Q6;
            Q6=makeQuery(id+"F3.opExtrude","SWEPT_FACE",FACE,{"disambiguationData":[OSD([sQuery(id+"F0.wireOp",EDGE,"E0.right")])]});
            var Q7;
            Q7=makeQuery(id+"F3.opExtrude","SWEPT_FACE",FACE,{"disambiguationData":[OSD([sQuery(id+"F0.wireOp",EDGE,"E0.top")])]});
            var Q8;
            Q8=makeQuery(id+"F4.opExtrude","CAP_EDGE",EDGE,{"disambiguationData":[OSD([sQuery(id+"F0.wireOp",EDGE,"E1.right")])],"isStart":true});
            var Q9;
            Q9=makeQuery(id+"F4.opExtrude","CAP_EDGE",EDGE,{"disambiguationData":[OSD([sQuery(id+"F0.wireOp",EDGE,"E1.top")])],"isStart":true});
            var Q10;
            Q10=makeQuery(id+"F4.opExtrude","CAP_EDGE",EDGE,{"disambiguationData":[OSD([sQuery(id+"F0.wireOp",EDGE,"E1.bottom")])],"isStart":true});
            var Q11;
            Q11=makeQuery(id+"F4.opExtrude","CAP_EDGE",EDGE,{"disambiguationData":[OSD([sQuery(id+"F0.wireOp",EDGE,"E1.left")])],"isStart":true});
            var Q12;
            Q12=makeQuery(id+"F2.opExtrude","CAP_EDGE",EDGE,{"disambiguationData":[OSD([sQuery(id+"F0.wireOp",EDGE,"E1.top")])],"isStart":true});
            var Q13;
            Q13=makeQuery(id+"F2.opExtrude","CAP_EDGE",EDGE,{"disambiguationData":[OSD([sQuery(id+"F0.wireOp",EDGE,"E1.right")])],"isStart":true});
            var Q14;
            Q14=makeQuery(id+"F2.opExtrude","CAP_EDGE",EDGE,{"disambiguationData":[OSD([sQuery(id+"F0.wireOp",EDGE,"E1.bottom")])],"isStart":true});
            var Q15;
            Q15=makeQuery(id+"F2.opExtrude","CAP_EDGE",EDGE,{"disambiguationData":[OSD([sQuery(id+"F0.wireOp",EDGE,"E1.left")])],"isStart":true});
            var Q16;
            Q16=makeQuery(id+"F2.opExtrude","SWEPT_EDGE",EDGE,{"disambiguationData":[OSD([sQuery(id+"F0.wireOp",EDGE,"E1.top"),sQuery(id+"F0.wireOp",EDGE,"E1.right")])]});
            var Q17;
            Q17=makeQuery(id+"F2.opExtrude","SWEPT_EDGE",EDGE,{"disambiguationData":[OSD([sQuery(id+"F0.wireOp",EDGE,"E1.bottom"),sQuery(id+"F0.wireOp",EDGE,"E1.right")])]});
            var Q18;
            Q18=makeQuery(id+"F2.opExtrude","SWEPT_EDGE",EDGE,{"disambiguationData":[OSD([sQuery(id+"F0.wireOp",EDGE,"E1.top"),sQuery(id+"F0.wireOp",EDGE,"E1.left")])]});
            var Q19;
            Q19=makeQuery(id+"F4.opExtrude","SWEPT_EDGE",EDGE,{"disambiguationData":[OSD([sQuery(id+"F0.wireOp",EDGE,"E1.top"),sQuery(id+"F0.wireOp",EDGE,"E1.left")])]});
            var Q20;
            Q20=makeQuery(id+"F4.opExtrude","SWEPT_EDGE",EDGE,{"disambiguationData":[OSD([sQuery(id+"F0.wireOp",EDGE,"E1.top"),sQuery(id+"F0.wireOp",EDGE,"E1.right")])]});
            var Q21;
            Q21=makeQuery(id+"F4.opExtrude","SWEPT_EDGE",EDGE,{"disambiguationData":[OSD([sQuery(id+"F0.wireOp",EDGE,"E1.bottom"),sQuery(id+"F0.wireOp",EDGE,"E1.right")])]});
            var Q22;
            Q22=makeQuery(id+"F2.opExtrude","SWEPT_EDGE",EDGE,{"disambiguationData":[OSD([sQuery(id+"F0.wireOp",EDGE,"E1.bottom"),sQuery(id+"F0.wireOp",EDGE,"E1.left")])]});
            var Q23;
            Q23=makeQuery(id+"F4.opExtrude","SWEPT_EDGE",EDGE,{"disambiguationData":[OSD([sQuery(id+"F0.wireOp",EDGE,"E1.bottom"),sQuery(id+"F0.wireOp",EDGE,"E1.left")])]});
            var Q24;
            Q24=makeQuery(id+"F2.opExtrude","CAP_EDGE",EDGE,{"disambiguationData":[OSD([sQuery(id+"F0.wireOp",EDGE,"E2.right")])],"isStart":true});
            var Q25;
            Q25=makeQuery(id+"F2.opExtrude","CAP_EDGE",EDGE,{"disambiguationData":[OSD([sQuery(id+"F0.wireOp",EDGE,"E2.top")])],"isStart":true});
            var Q26;
            Q26=makeQuery(id+"F2.opExtrude","CAP_EDGE",EDGE,{"disambiguationData":[OSD([sQuery(id+"F0.wireOp",EDGE,"E2.left")])],"isStart":true});
            var Q27;
            Q27=makeQuery(id+"F2.opExtrude","SWEPT_FACE",FACE,{"disambiguationData":[OSD([sQuery(id+"F0.wireOp",EDGE,"E2.bottom")])]});
            var Q28;
            Q28=makeQuery(id+"F4.opExtrude","CAP_EDGE",EDGE,{"disambiguationData":[OSD([sQuery(id+"F0.wireOp",EDGE,"E2.bottom")])],"isStart":true});
            var Q29;
            Q29=makeQuery(id+"F4.opExtrude","CAP_EDGE",EDGE,{"disambiguationData":[OSD([sQuery(id+"F0.wireOp",EDGE,"E2.right")])],"isStart":true});
            var Q30;
            Q30=makeQuery(id+"F4.opExtrude","CAP_EDGE",EDGE,{"disambiguationData":[OSD([sQuery(id+"F0.wireOp",EDGE,"E2.top")])],"isStart":true});
            var Q31;
            Q31=makeQuery(id+"F4.opExtrude","CAP_EDGE",EDGE,{"disambiguationData":[OSD([sQuery(id+"F0.wireOp",EDGE,"E2.left")])],"isStart":true});
            fillet(context, id + "F24", {"entities" : qUnion([Q0, Q1, Q2, Q3, Q4, Q5, Q6, Q7, Q8, Q9, Q10, Q11, Q12, Q13, Q14, Q15, Q16, Q17, Q18, Q19, Q20, Q21, Q22, Q23, Q24, Q25, Q26, Q27, Q28, Q29, Q30, Q31]), "radius" : 2.54 * mm, "tangentPropagation" : true, "allowEdgeOverflow" : false});
        }
        {
            var Q0;
            Q0=makeQuery(id+"F17.opExtrude","CAP_EDGE",EDGE,{"disambiguationData":[OSD([sQuery(id+"F14.wireOp",EDGE,"E28")])],"isStart":false});
            var Q1;
            {var subQ0=sQuery(id+"F14.wireOp",EDGE,"E29");var subQ1=sQuery(id+"F14.wireOp",EDGE,"E26");Q1=makeQuery(id+"F22.boolean.opBoolean","SPLIT",EDGE,{"disambiguationData":[TD([makeQuery(id+"F19.opExtrude","SWEPT_FACE",FACE,{"disambiguationData":[OSD([subQ1])]})])],"derivedFrom":makeQuery(id+"F19.opExtrude","CAP_EDGE",EDGE,{"disambiguationData":[OSD([subQ0])],"isStart":true})});}
            var Q2;
            Q2=makeQuery(id+"F19.opExtrude","CAP_EDGE",EDGE,{"disambiguationData":[OSD([sQuery(id+"F14.wireOp",EDGE,"E29")])],"isStart":false});
            var Q3;
            Q3=makeQuery(id+"F18.opExtrude","CAP_EDGE",EDGE,{"disambiguationData":[OSD([sQuery(id+"F14.wireOp",EDGE,"E29")])],"isStart":false});
            var Q4;
            {var subQ0=sQuery(id+"F14.wireOp",EDGE,"E29");var subQ1=sQuery(id+"F14.wireOp",EDGE,"E26");Q4=makeQuery(id+"F22.boolean.opBoolean","SPLIT",EDGE,{"disambiguationData":[TD([makeQuery(id+"F18.opExtrude","SWEPT_FACE",FACE,{"disambiguationData":[OSD([subQ1])]})])],"derivedFrom":makeQuery(id+"F18.opExtrude","CAP_EDGE",EDGE,{"disambiguationData":[OSD([subQ0])],"isStart":true})});}
            var Q5;
            Q5=makeQuery(id+"F17.opExtrude","CAP_EDGE",EDGE,{"disambiguationData":[OSD([sQuery(id+"F14.wireOp",EDGE,"E28")])],"isStart":true});
            var Q6;
            Q6=makeQuery(id+"F12.opExtrude","SWEPT_EDGE",EDGE,{"disambiguationData":[OSD([sQuery(id+"F5.wireOp",EDGE,"E11.top"),sQuery(id+"F5.wireOp",EDGE,"E11.right")])]});
            var Q7;
            Q7=makeQuery(id+"F12.opExtrude","SWEPT_EDGE",EDGE,{"disambiguationData":[OSD([sQuery(id+"F5.wireOp",EDGE,"E12.top"),sQuery(id+"F5.wireOp",EDGE,"E12.right")])]});
            var Q8;
            Q8=makeQuery(id+"F12.opExtrude","SWEPT_EDGE",EDGE,{"disambiguationData":[OSD([sQuery(id+"F5.wireOp",EDGE,"E7.right"),sQuery(id+"F5.wireOp",EDGE,"E7.bottom"),sQuery(id+"F5.wireOp",EDGE,"E12.right")])]});
            var Q9;
            Q9=makeQuery(id+"F12.opExtrude","SWEPT_EDGE",EDGE,{"disambiguationData":[OSD([sQuery(id+"F5.wireOp",EDGE,"E7.right"),sQuery(id+"F5.wireOp",EDGE,"E7.top"),sQuery(id+"F5.wireOp",EDGE,"E11.right")])]});
            var Q10;
            Q10=makeQuery(id+"F19.opExtrude","CAP_EDGE",EDGE,{"disambiguationData":[OSD([sQuery(id+"F14.wireOp",EDGE,"E34")])],"isStart":false});
            var Q11;
            {var subQ0=sQuery(id+"F14.wireOp",EDGE,"E34");var subQ1=sQuery(id+"F14.wireOp",EDGE,"E27");Q11=makeQuery(id+"F22.boolean.opBoolean","SPLIT",EDGE,{"disambiguationData":[TD([makeQuery(id+"F19.opExtrude","SWEPT_FACE",FACE,{"disambiguationData":[OSD([subQ1])]})])],"derivedFrom":makeQuery(id+"F19.opExtrude","CAP_EDGE",EDGE,{"disambiguationData":[OSD([subQ0])],"isStart":true})});}
            var Q12;
            {var subQ0=sQuery(id+"F14.wireOp",EDGE,"E34");var subQ1=sQuery(id+"F14.wireOp",EDGE,"E27");Q12=makeQuery(id+"F22.boolean.opBoolean","SPLIT",EDGE,{"disambiguationData":[TD([makeQuery(id+"F18.opExtrude","SWEPT_FACE",FACE,{"disambiguationData":[OSD([subQ1])]})])],"derivedFrom":makeQuery(id+"F18.opExtrude","CAP_EDGE",EDGE,{"disambiguationData":[OSD([subQ0])],"isStart":true})});}
            var Q13;
            Q13=makeQuery(id+"F18.opExtrude","CAP_EDGE",EDGE,{"disambiguationData":[OSD([sQuery(id+"F14.wireOp",EDGE,"E34")])],"isStart":false});
            var Q14;
            Q14=makeQuery(id+"F17.opExtrude","CAP_EDGE",EDGE,{"disambiguationData":[OSD([sQuery(id+"F14.wireOp",EDGE,"E33")])],"isStart":true});
            var Q15;
            Q15=makeQuery(id+"F17.opExtrude","CAP_EDGE",EDGE,{"disambiguationData":[OSD([sQuery(id+"F14.wireOp",EDGE,"E33")])],"isStart":false});
            var Q16;
            Q16=makeQuery(id+"F11.opExtrude","SWEPT_EDGE",EDGE,{"disambiguationData":[OSD([sQuery(id+"F6.wireOp",EDGE,"E16.bottom"),sQuery(id+"F6.wireOp",EDGE,"E16.right")])]});
            var Q17;
            Q17=makeQuery(id+"F11.opExtrude","SWEPT_EDGE",EDGE,{"disambiguationData":[OSD([sQuery(id+"F6.wireOp",EDGE,"E16.top"),sQuery(id+"F6.wireOp",EDGE,"E16.right")])]});
            var Q18;
            Q18=makeQuery(id+"F11.opExtrude","SWEPT_EDGE",EDGE,{"disambiguationData":[OSD([sQuery(id+"F6.wireOp",EDGE,"E15.top"),sQuery(id+"F6.wireOp",EDGE,"E15.left")])]});
            var Q19;
            Q19=makeQuery(id+"F11.opExtrude","SWEPT_EDGE",EDGE,{"disambiguationData":[OSD([sQuery(id+"F6.wireOp",EDGE,"E15.bottom"),sQuery(id+"F6.wireOp",EDGE,"E15.left")])]});
            var Q20;
            Q20=makeQuery(id+"F13.opFillet","BLEND_EDGE",EDGE,{"blendedFrom":[makeQuery(id+"F12.opExtrude","CAP_EDGE",EDGE,{"disambiguationData":[OSD([sQuery(id+"F5.wireOp",EDGE,"E9.left")])],"isStart":false}),makeQuery(id+"F12.opExtrude","SWEPT_FACE",FACE,{"disambiguationData":[OSD([sQuery(id+"F5.wireOp",EDGE,"E9.top")])]})],"blendedInto":[makeQuery(id+"F12.opExtrude","SWEPT_FACE",FACE,{"disambiguationData":[OSD([sQuery(id+"F5.wireOp",EDGE,"E9.top")])]})]});
            var Q21;
            Q21=makeQuery(id+"F13.opFillet","BLEND_EDGE",EDGE,{"blendedFrom":[makeQuery(id+"F12.opExtrude","CAP_EDGE",EDGE,{"disambiguationData":[OSD([sQuery(id+"F5.wireOp",EDGE,"E10.right")])],"isStart":false}),makeQuery(id+"F12.opExtrude","SWEPT_FACE",FACE,{"disambiguationData":[OSD([sQuery(id+"F5.wireOp",EDGE,"E10.top")])]})],"blendedInto":[makeQuery(id+"F12.opExtrude","SWEPT_FACE",FACE,{"disambiguationData":[OSD([sQuery(id+"F5.wireOp",EDGE,"E10.top")])]})]});
            var Q22;
            Q22=makeQuery(id+"F12.opExtrude","SWEPT_EDGE",EDGE,{"disambiguationData":[OSD([sQuery(id+"F5.wireOp",EDGE,"E6.right"),sQuery(id+"F5.wireOp",EDGE,"E9.bottom"),sQuery(id+"F5.wireOp",EDGE,"E9.left")])]});
            var Q23;
            Q23=makeQuery(id+"F12.opExtrude","SWEPT_EDGE",EDGE,{"disambiguationData":[OSD([sQuery(id+"F5.wireOp",EDGE,"E6.right"),sQuery(id+"F5.wireOp",EDGE,"E10.bottom"),sQuery(id+"F5.wireOp",EDGE,"E10.left")])]});
            fillet(context, id + "F25", {"entities" : qUnion([Q0, Q1, Q2, Q3, Q4, Q5, Q6, Q7, Q8, Q9, Q10, Q11, Q12, Q13, Q14, Q15, Q16, Q17, Q18, Q19, Q20, Q21, Q22, Q23]), "radius" : 0.64 * mm, "tangentPropagation" : true, "allowEdgeOverflow" : false});
        }
        {
            var Q0;
            Q0=makeQuery(id+"F10.opExtrude","CAP_EDGE",EDGE,{"disambiguationData":[OSD([sQuery(id+"F6.wireOp",EDGE,"E14")])],"isStart":false});
            var Q1;
            Q1=makeQuery(id+"F10.opExtrude","CAP_EDGE",EDGE,{"disambiguationData":[OSD([sQuery(id+"F6.wireOp",EDGE,"E13")])],"isStart":true});
            var Q2;
            Q2=makeQuery(id+"F16.opExtrude","CAP_EDGE",EDGE,{"disambiguationData":[OSD([sQuery(id+"F5.wireOp",EDGE,"E4")])],"isStart":true});
            var Q3;
            Q3=makeQuery(id+"F9.opExtrude","CAP_EDGE",EDGE,{"disambiguationData":[OSD([sQuery(id+"F5.wireOp",EDGE,"E4")])],"isStart":true});
            var Q4;
            Q4=makeQuery(id+"F7.opExtrude","CAP_EDGE",EDGE,{"disambiguationData":[OSD([sQuery(id+"F5.wireOp",EDGE,"E3")])],"isStart":false});
            var Q5;
            Q5=makeQuery(id+"F15.opExtrude","CAP_EDGE",EDGE,{"disambiguationData":[OSD([sQuery(id+"F5.wireOp",EDGE,"E3")])],"isStart":false});
            var Q6;
            Q6=makeQuery(id+"F12.opExtrude","CAP_EDGE",EDGE,{"disambiguationData":[OSD([sQuery(id+"F5.wireOp",EDGE,"E9.left")])],"isStart":true});
            var Q7;
            Q7=makeQuery(id+"F12.opExtrude","CAP_EDGE",EDGE,{"disambiguationData":[OSD([sQuery(id+"F5.wireOp",EDGE,"E9.top")])],"isStart":true});
            var Q8;
            Q8=makeQuery(id+"F12.opExtrude","CAP_EDGE",EDGE,{"disambiguationData":[OSD([sQuery(id+"F5.wireOp",EDGE,"E12.left")])],"isStart":true});
            var Q9;
            Q9=makeQuery(id+"F12.opExtrude","CAP_EDGE",EDGE,{"disambiguationData":[OSD([sQuery(id+"F5.wireOp",EDGE,"E12.top")])],"isStart":true});
            var Q10;
            Q10=makeQuery(id+"F12.opExtrude","CAP_EDGE",EDGE,{"disambiguationData":[OSD([sQuery(id+"F5.wireOp",EDGE,"E9.right")])],"isStart":true});
            var Q11;
            Q11=makeQuery(id+"F12.opExtrude","CAP_EDGE",EDGE,{"disambiguationData":[OSD([sQuery(id+"F5.wireOp",EDGE,"E12.right")])],"isStart":true});
            var Q12;
            Q12=makeQuery(id+"F12.opExtrude","CAP_EDGE",EDGE,{"disambiguationData":[OSD([sQuery(id+"F5.wireOp",EDGE,"E10.left")])],"isStart":true});
            var Q13;
            Q13=makeQuery(id+"F12.opExtrude","CAP_EDGE",EDGE,{"disambiguationData":[OSD([sQuery(id+"F5.wireOp",EDGE,"E10.top")])],"isStart":true});
            var Q14;
            Q14=makeQuery(id+"F12.opExtrude","CAP_EDGE",EDGE,{"disambiguationData":[OSD([sQuery(id+"F5.wireOp",EDGE,"E11.left")])],"isStart":true});
            var Q15;
            Q15=makeQuery(id+"F12.opExtrude","CAP_EDGE",EDGE,{"disambiguationData":[OSD([sQuery(id+"F5.wireOp",EDGE,"E11.top")])],"isStart":true});
            var Q16;
            Q16=makeQuery(id+"F12.opExtrude","CAP_EDGE",EDGE,{"disambiguationData":[OSD([sQuery(id+"F5.wireOp",EDGE,"E9.bottom")])],"isStart":true});
            var Q17;
            Q17=makeQuery(id+"F12.opExtrude","CAP_EDGE",EDGE,{"disambiguationData":[OSD([sQuery(id+"F5.wireOp",EDGE,"E11.right")])],"isStart":true});
            var Q18;
            Q18=makeQuery(id+"F12.opExtrude","CAP_EDGE",EDGE,{"disambiguationData":[OSD([sQuery(id+"F5.wireOp",EDGE,"E10.right")])],"isStart":true});
            var Q19;
            Q19=makeQuery(id+"F12.opExtrude","CAP_EDGE",EDGE,{"disambiguationData":[OSD([sQuery(id+"F5.wireOp",EDGE,"E7.bottom")])],"isStart":true});
            var Q20;
            Q20=makeQuery(id+"F12.opExtrude","CAP_EDGE",EDGE,{"disambiguationData":[OSD([sQuery(id+"F5.wireOp",EDGE,"E10.bottom")])],"isStart":true});
            var Q21;
            Q21=makeQuery(id+"F12.opExtrude","CAP_EDGE",EDGE,{"disambiguationData":[OSD([sQuery(id+"F5.wireOp",EDGE,"E7.top")])],"isStart":true});
            fillet(context, id + "F26", {"entities" : qUnion([Q0, Q1, Q2, Q3, Q4, Q5, Q6, Q7, Q8, Q9, Q10, Q11, Q12, Q13, Q14, Q15, Q16, Q17, Q18, Q19, Q20, Q21]), "radius" : 1.27 * mm, "tangentPropagation" : true, "allowEdgeOverflow" : false});
        }
    });
